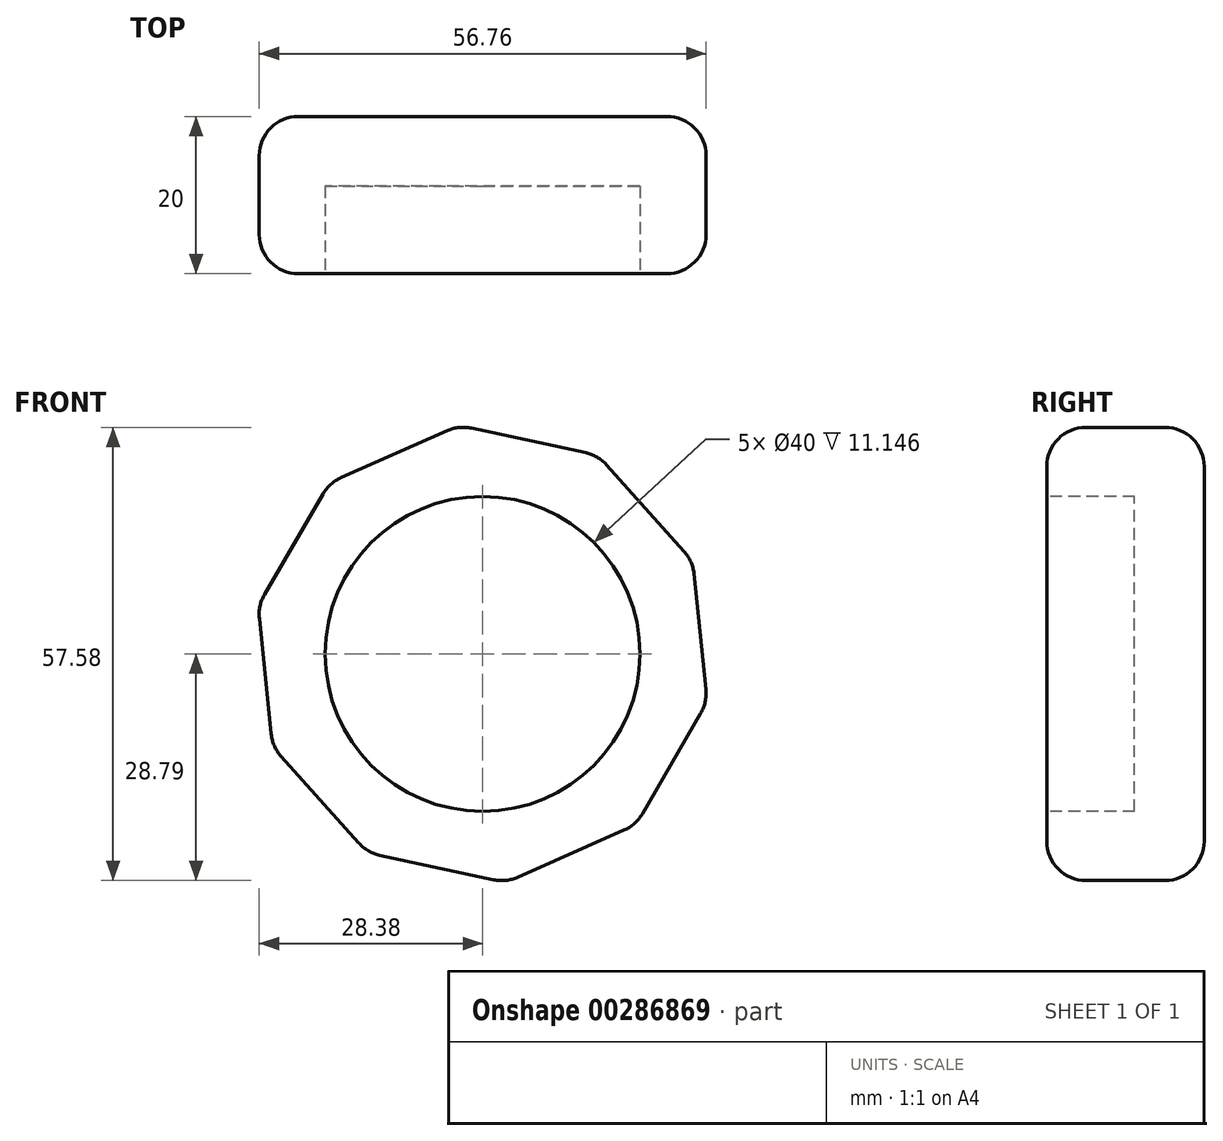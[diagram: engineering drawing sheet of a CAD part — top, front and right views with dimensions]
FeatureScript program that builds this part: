
annotation { "Feature Type Name" : "Feature", "Feature Type Description" : "" }
export const myFeature = defineFeature(function(context is Context, id is Id, definition is map)
    precondition{}
    {
        {
            var Q0;
            Q0=qCreatedBy(makeId("Front.planeOp"),FACE);
            var sketch = newSketch(context, id + "F0", { "sketchPlane" : qUnion([Q0])});
            skCircle(sketch, "E0.cCircle", {"center": v(0, 0) * mm, "radius": 29.17 * mm, "construction": true});
            skLineSegment(sketch, "E0.0", {"start": v(14.65, 25.23) * mm, "end": v(26.68, 11.8) * mm});
            skLineSegment(sketch, "E0.1", {"start": v(26.68, 11.8) * mm, "end": v(28.52, -6.13) * mm});
            skLineSegment(sketch, "E0.2", {"start": v(28.52, -6.13) * mm, "end": v(19.47, -21.73) * mm});
            skLineSegment(sketch, "E0.3", {"start": v(19.47, -21.73) * mm, "end": v(2.98, -29.02) * mm});
            skLineSegment(sketch, "E0.4", {"start": v(2.98, -29.02) * mm, "end": v(-14.65, -25.23) * mm});
            skLineSegment(sketch, "E0.5", {"start": v(-14.65, -25.23) * mm, "end": v(-26.68, -11.8) * mm});
            skLineSegment(sketch, "E0.6", {"start": v(-26.68, -11.8) * mm, "end": v(-28.52, 6.13) * mm});
            skLineSegment(sketch, "E0.7", {"start": v(-28.52, 6.13) * mm, "end": v(-19.47, 21.73) * mm});
            skLineSegment(sketch, "E0.8", {"start": v(-19.47, 21.73) * mm, "end": v(-2.98, 29.02) * mm});
            skLineSegment(sketch, "E0.9", {"start": v(-2.98, 29.02) * mm, "end": v(14.65, 25.23) * mm});
            skSolve(sketch);
        }
        {
            var Q0;
            Q0 = qSketchRegion(id + "F0", true);
            extrude(context, id + "F1", {"entities" : qUnion([Q0]), "depth" : 20 * mm});
        }
        {
            var Q0;
            Q0=makeQuery(id+"F1.opExtrude","CAP_FACE",FACE,{"disambiguationData":[OSD([sQuery(id+"F0.wireOp",EDGE,"E0.0"),sQuery(id+"F0.wireOp",EDGE,"E0.1"),sQuery(id+"F0.wireOp",EDGE,"E0.2"),sQuery(id+"F0.wireOp",EDGE,"E0.3"),sQuery(id+"F0.wireOp",EDGE,"E0.4"),sQuery(id+"F0.wireOp",EDGE,"E0.5"),sQuery(id+"F0.wireOp",EDGE,"E0.6"),sQuery(id+"F0.wireOp",EDGE,"E0.7"),sQuery(id+"F0.wireOp",EDGE,"E0.8"),sQuery(id+"F0.wireOp",EDGE,"E0.9")])],"isStart":false});
            var sketch = newSketch(context, id + "F2", { "sketchPlane" : qUnion([Q0])});
            skCircle(sketch, "E1", {"center": v(0, 0) * mm, "radius": 20 * mm});
            skSolve(sketch);
        }
        {
            var Q0;
            Q0=makeQuery(id+"F2.imprint","IMPRINT",FACE,{"disambiguationData":[TD([[makeQuery(id+"F2.imprint","IMPRINT",EDGE,{"derivedFrom":sQuery(id+"F2.wireOp",EDGE,"E1")}),1.0]])]});
            extrude(context, id + "F3", {"entities" : qUnion([Q0]), "operationType" : NewBodyOperationType.REMOVE, "oppositeDirection" : true, "depth" : 11.15 * mm});
        }
        {
            var Q0;
            Q0=makeQuery(id+"F1.opExtrude","CAP_EDGE",EDGE,{"disambiguationData":[OSD([sQuery(id+"F0.wireOp",EDGE,"E0.8")])],"isStart":true});
            var Q1;
            Q1=makeQuery(id+"F1.opExtrude","SWEPT_FACE",FACE,{"disambiguationData":[OSD([sQuery(id+"F0.wireOp",EDGE,"E0.7")])]});
            var Q2;
            Q2=makeQuery(id+"F1.opExtrude","SWEPT_FACE",FACE,{"disambiguationData":[OSD([sQuery(id+"F0.wireOp",EDGE,"E0.6")])]});
            var Q3;
            Q3=makeQuery(id+"F1.opExtrude","CAP_EDGE",EDGE,{"disambiguationData":[OSD([sQuery(id+"F0.wireOp",EDGE,"E0.5")])],"isStart":true});
            var Q4;
            Q4=makeQuery(id+"F1.opExtrude","SWEPT_FACE",FACE,{"disambiguationData":[OSD([sQuery(id+"F0.wireOp",EDGE,"E0.4")])]});
            var Q5;
            Q5=makeQuery(id+"F1.opExtrude","SWEPT_FACE",FACE,{"disambiguationData":[OSD([sQuery(id+"F0.wireOp",EDGE,"E0.3")])]});
            var Q6;
            Q6=makeQuery(id+"F1.opExtrude","SWEPT_FACE",FACE,{"disambiguationData":[OSD([sQuery(id+"F0.wireOp",EDGE,"E0.2")])]});
            var Q7;
            Q7=makeQuery(id+"F1.opExtrude","SWEPT_FACE",FACE,{"disambiguationData":[OSD([sQuery(id+"F0.wireOp",EDGE,"E0.1")])]});
            var Q8;
            Q8=makeQuery(id+"F1.opExtrude","SWEPT_FACE",FACE,{"disambiguationData":[OSD([sQuery(id+"F0.wireOp",EDGE,"E0.0")])]});
            var Q9;
            Q9=makeQuery(id+"F1.opExtrude","SWEPT_FACE",FACE,{"disambiguationData":[OSD([sQuery(id+"F0.wireOp",EDGE,"E0.9")])]});
            var Q10;
            Q10=makeQuery(id+"F1.opExtrude","SWEPT_FACE",FACE,{"disambiguationData":[OSD([sQuery(id+"F0.wireOp",EDGE,"E0.8")])]});
            var Q11;
            Q11=makeQuery(id+"F1.opExtrude","SWEPT_FACE",FACE,{"disambiguationData":[OSD([sQuery(id+"F0.wireOp",EDGE,"E0.5")])]});
            fillet(context, id + "F4", {"entities" : qUnion([Q0, Q1, Q2, Q3, Q4, Q5, Q6, Q7, Q8, Q9, Q10, Q11]), "radius" : 5 * mm, "tangentPropagation" : true, "allowEdgeOverflow" : false});
        }
    });
